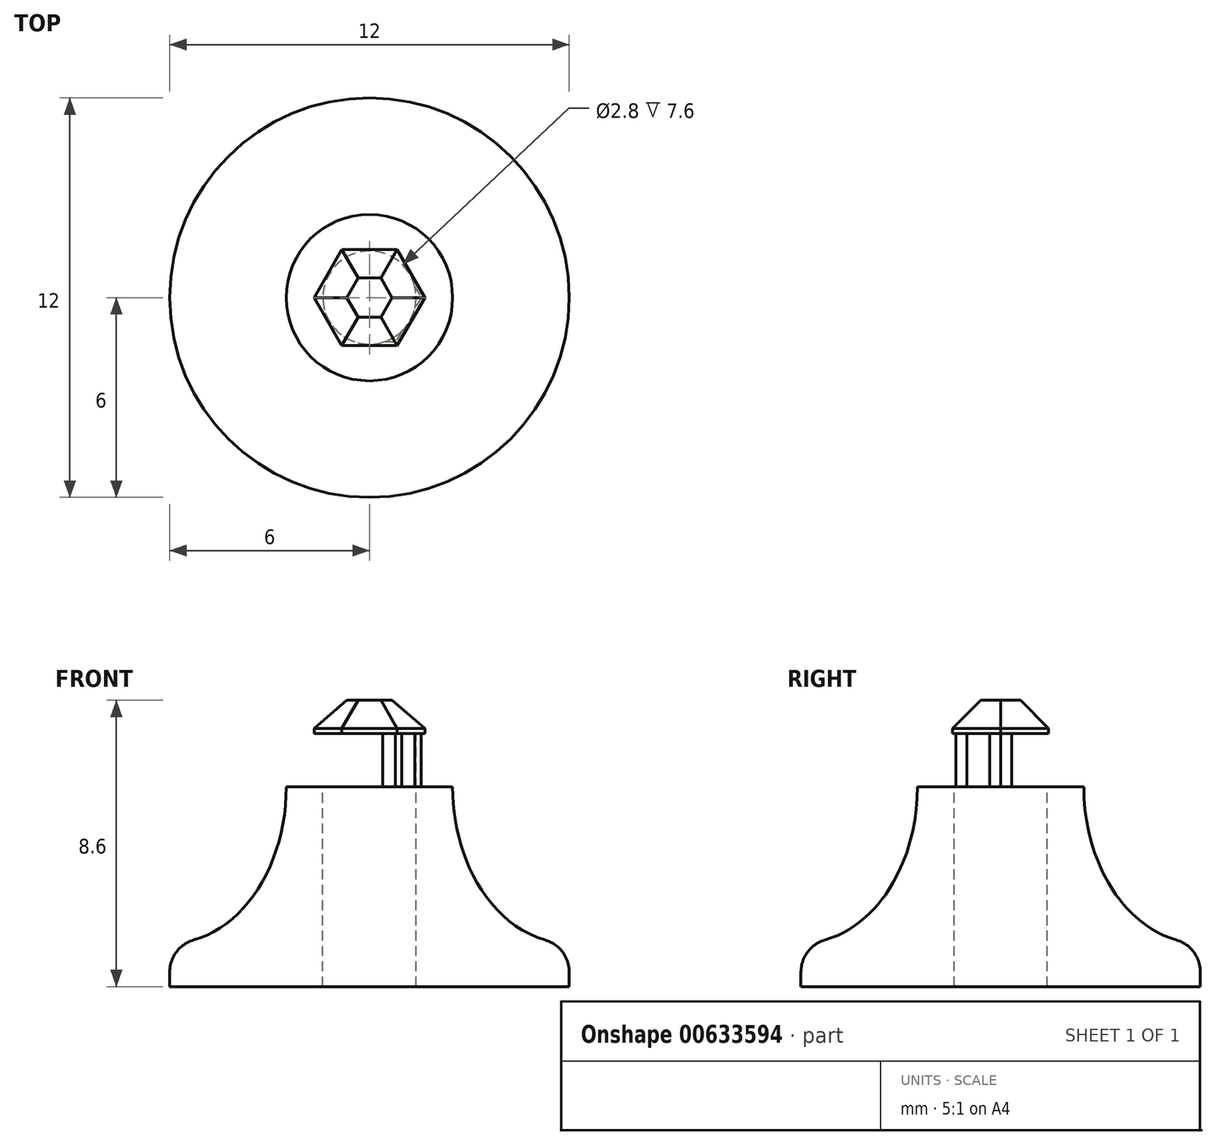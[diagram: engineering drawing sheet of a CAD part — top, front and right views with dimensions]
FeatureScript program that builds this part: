
annotation { "Feature Type Name" : "Feature", "Feature Type Description" : "" }
export const myFeature = defineFeature(function(context is Context, id is Id, definition is map)
    precondition{}
    {
        {
            var Q0;
            Q0=qCreatedBy(makeId("Front.planeOp"),FACE);
            var sketch = newSketch(context, id + "F0", { "sketchPlane" : qUnion([Q0])});
            skLineSegment(sketch, "E0.bottom", {"start": v(0, 0) * mm, "end": v(6, 0) * mm});
            skLineSegment(sketch, "E0.top", {"start": v(0, 6) * mm, "end": v(2.5, 6) * mm});
            skLineSegment(sketch, "E0.left", {"start": v(0, 0) * mm, "end": v(0, 6) * mm});
            skLineSegment(sketch, "E0.right", {"start": v(6, 0) * mm, "end": v(6, 0.44) * mm});
            skEllipticalArc(sketch, "E1", {});
            skPoint(sketch, "E2", {"position": v(2.5, 6) * mm});
            skPoint(sketch, "E3", {"position": v(6, 1.3) * mm});
            skPoint(sketch, "E4.visualSharp", {"position": v(0, 6) * mm});
            skArc(sketch, "E5.filletArc", {"start": v(6, 0.44) * mm, "mid": v(5.8, 1.04) * mm, "end": v(5.27, 1.4) * mm});
            const initialGuessF0  = {"E1": [0.006, 0.006, -1, 0, 0.0035, 0.0047, 6.283185307179586, 1.3618196011728392]};
            skSetInitialGuess(sketch, initialGuessF0);
            skSolve(sketch);
        }
        {
            var Q0;
            Q0=makeQuery(id+"F0.imprint","IMPRINT",FACE,{"disambiguationData":[TD([[makeQuery(id+"F0.imprint","IMPRINT",EDGE,{"derivedFrom":sQuery(id+"F0.wireOp",EDGE,"E0.bottom")}),1.0]])]});
            var Q1;
            Q1=sQuery(id+"F0.wireOp",EDGE,"E0.left");
            revolve(context, id + "F1", {"entities" : qUnion([Q0]), "axis" : qUnion([Q1]), "revolveType" : RevolveType.FULL});
        }
        {
            var Q0;
            Q0=makeQuery(id+"F1.opRevolve","SWEPT_BODY",BODY,{"disambiguationData":[OSD([sQuery(id+"F0.wireOp",EDGE,"E0.bottom"),sQuery(id+"F0.wireOp",EDGE,"E0.top"),sQuery(id+"F0.wireOp",EDGE,"E0.left"),sQuery(id+"F0.wireOp",EDGE,"E0.right"),sQuery(id+"F0.wireOp",EDGE,"E1"),sQuery(id+"F0.wireOp",EDGE,"ArTpo5st-Iq33-hNdW-1lph-2rlKh8i0XKDo"),sQuery(id+"F0.wireOp",EDGE,"E5.filletArc")])]});
            transform(context, id + "F2", {"entities" : qUnion([Q0]), "transformType" : TransformType.TRANSLATION_3D, "dx" : 0 * mm, "dy" : 0 * mm, "dz" : 0 * mm, "makeCopy" : true});
        }
        {
            var Q0;
            Q0=makeQuery(id+"F1.opRevolve","SWEPT_FACE",FACE,{"disambiguationData":[OSD([sQuery(id+"F0.wireOp",EDGE,"E0.top")])]});
            var sketch = newSketch(context, id + "F3", { "sketchPlane" : qUnion([Q0])});
            skCircle(sketch, "E6", {"center": v(0, 0) * mm, "radius": 1.4 * mm});
            skSolve(sketch);
        }
        {
            var Q0;
            Q0=makeQuery(id+"F3.imprint","IMPRINT",FACE,{"disambiguationData":[TD([[makeQuery(id+"F3.imprint","IMPRINT",EDGE,{"derivedFrom":sQuery(id+"F3.wireOp",EDGE,"E6")}),1.0]])]});
            extrude(context, id + "F4", {"entities" : qUnion([Q0]), "operationType" : NewBodyOperationType.REMOVE, "endBound" : BoundingType.THROUGH_ALL, "oppositeDirection" : true, "depth" : 25 * mm});
        }
        {
            var Q0;
            Q0=makeQuery(id+"F2.opPattern","COPY",FACE,{"derivedFrom":makeQuery(id+"F1.opRevolve","SWEPT_FACE",FACE,{"disambiguationData":[OSD([sQuery(id+"F0.wireOp",EDGE,"E0.top")])]}),"instanceName":"1"});
            var sketch = newSketch(context, id + "F5", { "sketchPlane" : qUnion([Q0])});
            skCircle(sketch, "E7.cCircle", {"center": v(0, 0) * mm, "radius": 1.34 * mm, "construction": true});
            skLineSegment(sketch, "E7.0", {"start": v(1.55, 0) * mm, "end": v(0.77, -1.34) * mm});
            skLineSegment(sketch, "E7.1", {"start": v(0.77, -1.34) * mm, "end": v(-0.78, -1.34) * mm});
            skLineSegment(sketch, "E7.2", {"start": v(-0.78, -1.34) * mm, "end": v(-1.55, 0) * mm});
            skLineSegment(sketch, "E7.3", {"start": v(-1.55, 0) * mm, "end": v(-0.77, 1.34) * mm});
            skLineSegment(sketch, "E7.4", {"start": v(-0.77, 1.34) * mm, "end": v(0.78, 1.34) * mm});
            skLineSegment(sketch, "E7.5", {"start": v(0.78, 1.34) * mm, "end": v(1.55, 0) * mm});
            skPoint(sketch, "E7.0.midPoint", {"position": v(1.16, -0.67) * mm});
            skSolve(sketch);
        }
        {
            var Q0;
            Q0=makeQuery(id+"F5.imprint","IMPRINT",FACE,{"disambiguationData":[TD([[makeQuery(id+"F5.imprint","IMPRINT",EDGE,{"derivedFrom":sQuery(id+"F5.wireOp",EDGE,"E7.0")}),-1.0]])]});
            extrude(context, id + "F6", {"entities" : qUnion([Q0]), "operationType" : NewBodyOperationType.ADD, "depth" : 1.6 * mm});
        }
        {
            var Q0;
            Q0=makeQuery(id+"F6.opExtrude","CAP_FACE",FACE,{"disambiguationData":[OSD([sQuery(id+"F5.wireOp",EDGE,"E7.0"),sQuery(id+"F5.wireOp",EDGE,"E7.1"),sQuery(id+"F5.wireOp",EDGE,"E7.2"),sQuery(id+"F5.wireOp",EDGE,"E7.3"),sQuery(id+"F5.wireOp",EDGE,"E7.4"),sQuery(id+"F5.wireOp",EDGE,"E7.5")])],"isStart":false});
            var sketch = newSketch(context, id + "F7", { "sketchPlane" : qUnion([Q0])});
            skLineSegment(sketch, "E8.0", {"start": v(-1.67, 0) * mm, "end": v(-0.83, 1.44) * mm});
            skLineSegment(sketch, "E8.1", {"start": v(0.83, 1.44) * mm, "end": v(1.67, 0) * mm});
            skLineSegment(sketch, "E8.2", {"start": v(1.67, 0) * mm, "end": v(0.83, -1.44) * mm});
            skLineSegment(sketch, "E8.3", {"start": v(-0.83, 1.44) * mm, "end": v(0.83, 1.44) * mm});
            skLineSegment(sketch, "E8.4", {"start": v(0.83, -1.44) * mm, "end": v(-0.83, -1.44) * mm});
            skLineSegment(sketch, "E8.5", {"start": v(-0.83, -1.44) * mm, "end": v(-1.67, 0) * mm});
            skSolve(sketch);
        }
        {
            var Q0;
            Q0=qSketchRegion(id+"F7",true);
            extrude(context, id + "F8", {"entities" : qUnion([Q0]), "operationType" : NewBodyOperationType.ADD, "depth" : 1 * mm});
        }
        {
            var Q0;
            Q0=makeQuery(id+"F8.opExtrude","CAP_EDGE",EDGE,{"disambiguationData":[OSD([sQuery(id+"F7.wireOp",EDGE,"E8.5")])],"isStart":false});
            var Q1;
            Q1=makeQuery(id+"F8.opExtrude","CAP_EDGE",EDGE,{"disambiguationData":[OSD([sQuery(id+"F7.wireOp",EDGE,"E8.4")])],"isStart":false});
            var Q2;
            Q2=makeQuery(id+"F8.opExtrude","CAP_EDGE",EDGE,{"disambiguationData":[OSD([sQuery(id+"F7.wireOp",EDGE,"E8.0")])],"isStart":false});
            var Q3;
            Q3=makeQuery(id+"F8.opExtrude","CAP_EDGE",EDGE,{"disambiguationData":[OSD([sQuery(id+"F7.wireOp",EDGE,"E8.3")])],"isStart":false});
            var Q4;
            Q4=makeQuery(id+"F8.opExtrude","CAP_EDGE",EDGE,{"disambiguationData":[OSD([sQuery(id+"F7.wireOp",EDGE,"E8.1")])],"isStart":false});
            var Q5;
            Q5=makeQuery(id+"F8.opExtrude","CAP_EDGE",EDGE,{"disambiguationData":[OSD([sQuery(id+"F7.wireOp",EDGE,"E8.2")])],"isStart":false});
            chamfer(context, id + "F9", {"entities" : qUnion([Q0, Q1, Q2, Q3, Q4, Q5]), "width" : 0.85 * mm});
        }
    });
